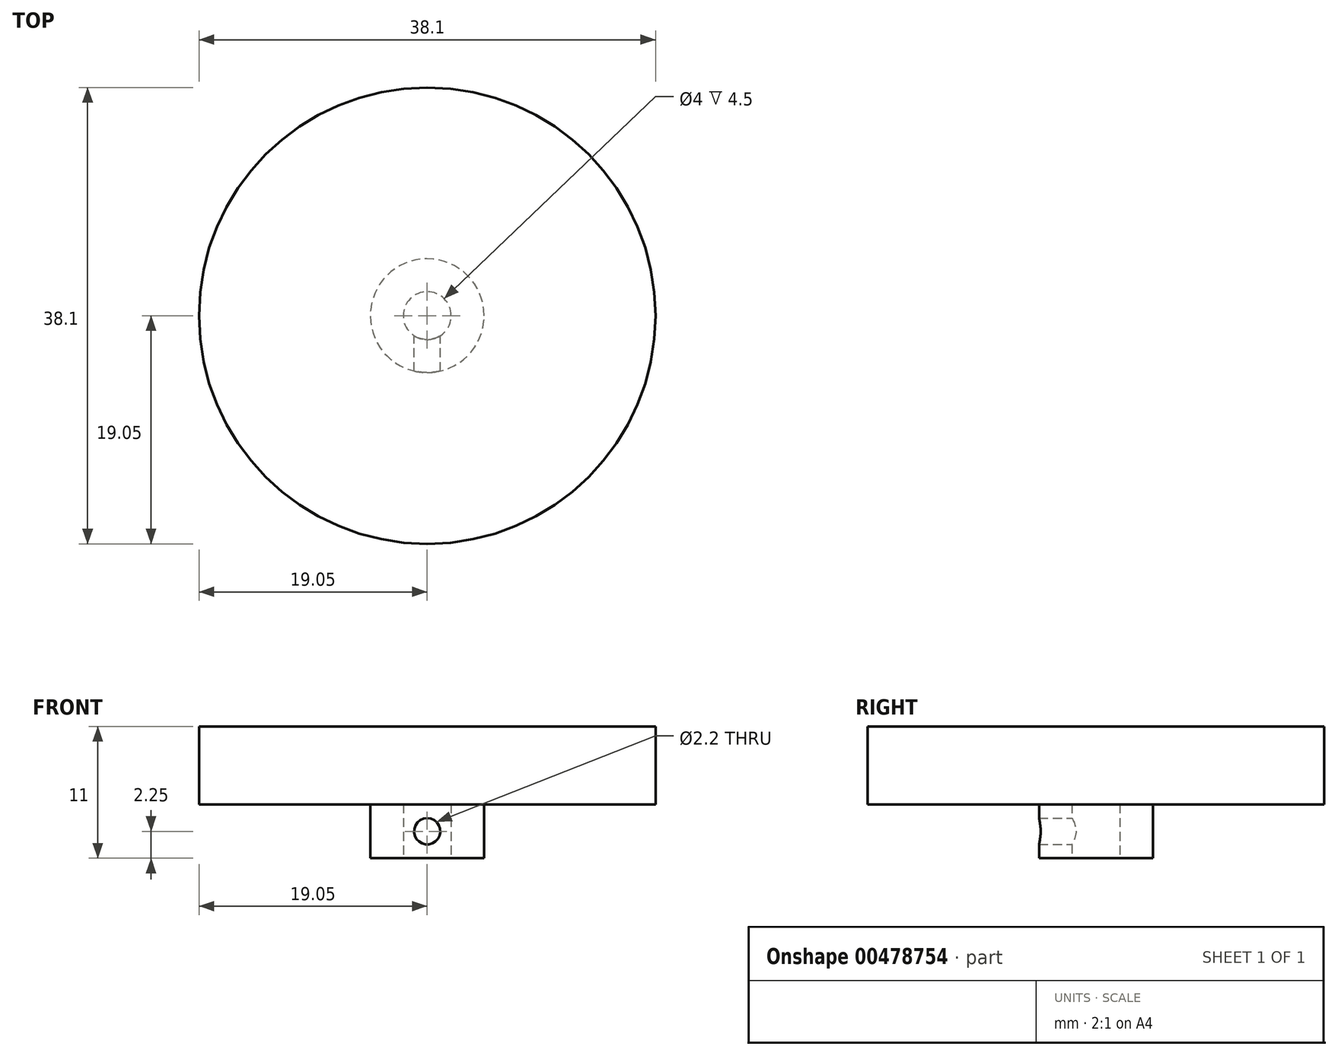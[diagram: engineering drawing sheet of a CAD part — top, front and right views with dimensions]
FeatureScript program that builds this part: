
annotation { "Feature Type Name" : "Feature", "Feature Type Description" : "" }
export const myFeature = defineFeature(function(context is Context, id is Id, definition is map)
    precondition{}
    {
        {
            var Q0;
            Q0=qCreatedBy(makeId("Top.planeOp"),FACE);
            var sketch = newSketch(context, id + "F0", { "sketchPlane" : qUnion([Q0])});
            skCircle(sketch, "E0", {"center": v(0, 0) * mm, "radius": 19.05 * mm});
            skCircle(sketch, "E1", {"center": v(0, 0) * mm, "radius": 4.75 * mm});
            skSolve(sketch);
        }
        {
            var Q0;
            Q0=makeQuery(id+"F0.imprint","IMPRINT",FACE,{"disambiguationData":[TD([[makeQuery(id+"F0.imprint","IMPRINT",EDGE,{"derivedFrom":sQuery(id+"F0.wireOp",EDGE,"E0")}),1.0]])]});
            var Q1;
            Q1=makeQuery(id+"F0.imprint","IMPRINT",FACE,{"disambiguationData":[TD([[makeQuery(id+"F0.imprint","IMPRINT",EDGE,{"derivedFrom":sQuery(id+"F0.wireOp",EDGE,"E1")}),1.0]])]});
            extrude(context, id + "F1", {"entities" : qUnion([Q0, Q1]), "depth" : 6.5 * mm});
        }
        {
            var Q0;
            Q0=makeQuery(id+"F0.imprint","IMPRINT",FACE,{"disambiguationData":[TD([[makeQuery(id+"F0.imprint","IMPRINT",EDGE,{"derivedFrom":sQuery(id+"F0.wireOp",EDGE,"E1")}),1.0]])]});
            extrude(context, id + "F2", {"entities" : qUnion([Q0]), "operationType" : NewBodyOperationType.ADD, "oppositeDirection" : true, "depth" : 4.5 * mm});
        }
        {
            var Q0;
            Q0=makeQuery(id+"F2.opExtrude","CAP_FACE",FACE,{"disambiguationData":[OSD([sQuery(id+"F0.wireOp",EDGE,"E1")])],"isStart":false});
            var sketch = newSketch(context, id + "F3", { "sketchPlane" : qUnion([Q0])});
            skCircle(sketch, "E2", {"center": v(0, 0) * mm, "radius": 2 * mm});
            skSolve(sketch);
        }
        {
            var Q0;
            Q0=makeQuery(id+"F3.imprint","IMPRINT",FACE,{"disambiguationData":[TD([[makeQuery(id+"F3.imprint","IMPRINT",EDGE,{"derivedFrom":sQuery(id+"F3.wireOp",EDGE,"E2")}),1.0]])]});
            extrude(context, id + "F4", {"entities" : qUnion([Q0]), "operationType" : NewBodyOperationType.REMOVE, "oppositeDirection" : true, "depth" : 4.5 * mm});
        }
        {
            var Q0;
            Q0=qCreatedBy(makeId("Front.planeOp"),FACE);
            var sketch = newSketch(context, id + "F5", { "sketchPlane" : qUnion([Q0])});
            skCircle(sketch, "E3", {"center": v(0, -2.25) * mm, "radius": 1.1 * mm});
            skSolve(sketch);
        }
        {
            var Q0;
            Q0=makeQuery(id+"F5.imprint","IMPRINT",FACE,{"disambiguationData":[TD([[makeQuery(id+"F5.imprint","IMPRINT",EDGE,{"derivedFrom":sQuery(id+"F5.wireOp",EDGE,"E3")}),1.0]])]});
            extrude(context, id + "F6", {"entities" : qUnion([Q0]), "operationType" : NewBodyOperationType.REMOVE, "depth" : 5 * mm});
        }
    });
